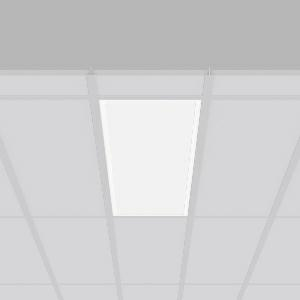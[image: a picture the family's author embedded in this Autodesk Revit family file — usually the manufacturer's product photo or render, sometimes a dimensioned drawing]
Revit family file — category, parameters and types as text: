
# Revit family: sidelite_eco_672371_002_07_c58a
name_source: partatom
category: Lighting Fixtures
units: mm (PartAtom-declared; Revit-internal decimal feet)

## family parameters
Cut with Voids When Loaded = No
Host = Face
Light Source = No
Part Type = Normal
Room Calculation Point = No
Round Connector Dimension = Use Diameter
Shared = No

## types (1)
- SIDELITE ECO (1 x LED Modul 830, 3300 lm, 3000)
    Apparent Load = 29 VA
    CIE Flux Codes = 46 79 96 100 100
    Color Rendering = 80
    Color Temperature = 3000
    Default Elevation = 1800 mm
    Description = Series: SIDELITE ECO
Highly economical recessed luminaire with progressive LED technology. For escape route illumination. Frame made of aluminium, powder-coated. Diffuser: plastic, opal. Lightguide and diffuser made of non-yellowing plastic (PMMA). Lateral light emission (RZB SIDELITE technology) for homogeneous light distribution. External driver. Self-contained system with automatic self-test and feedback via DALI bus, only to RZB DALI monitoring system. External driver with simple plug-in locking system. Extended connection cable (1.90 m). 
Colour: white
Length: 1195 mm
Width: 295 mm
Cut-out length: 1170 mm
Cut-out width: 270 mm
Recess height: 160 mm
Luminaire: recess height: 40 mm
Weight: 4.4 kg
Operating mode: maintained power mode
Duration time: 3 h
Lamp: LED
Socket: without socket
Colour temperature: 3000K
Colour rendering index (CRI): 80
System power: 29 W
Rated luminous flux: 3300 lm
Luminous flux, emergency: 480 lm
System power, emergency: -
Control gear: Regulated power supply
Protection class: I
Type of protection: IP 40
    Height = 0 mm  [stored 0 ft]
    Lamp = 1 x LED Modul 830
    Lamp Light Flux = 3300 lm
    Lamp count = 1
    Length = 1195 mm
    Lifetime = 50000 h
    Luminous efficacy = 114 lm/W
    Manufacturer = RZB
    ModVariant = No
    Model = 672371.002.07
    Mounting Place = Ceiling
    Mounting Type = Recessed
    Number of Poles = 1
    OnlyDefault = Yes
    Power Factor = 1
    Product Name = SIDELITE ECO
    Product group = Recessed modular luminaires
    ProductGroupID = 406
    Protection Class = Protection class I
    Protection Degree = IP 40
    RLX_Detail_Level = 1
    RLX_Emergency_Light_Flux = 480 lm
    RLX_Emergency_Type = 3
    RLX_Emergency_Type_DB = Yes
    RlxData = <blob elided: 30693 chars, md5=d7f2a410>
    Socket = socket
    Standby Power = 0 W
    System Light Flux = 3300 lm
    System Power = 29 W
    Type Comments = Product without accessories
    Type Image = 312365.002.jpg
    URL = http://relux.com
    VarID = ---
    Voltage = 230 V
    Voltage Range = 220-240 V
    Weight = 0.00 kg
    Width = 295 mm

note: [stored X ft] marks values corroborated as IEEE doubles in the binary element streams (Revit-internal decimal feet)

## geometry (parser evidence)
native form markers: Blend x4, Sweep x13
no freeform markers — native parametric forms only
